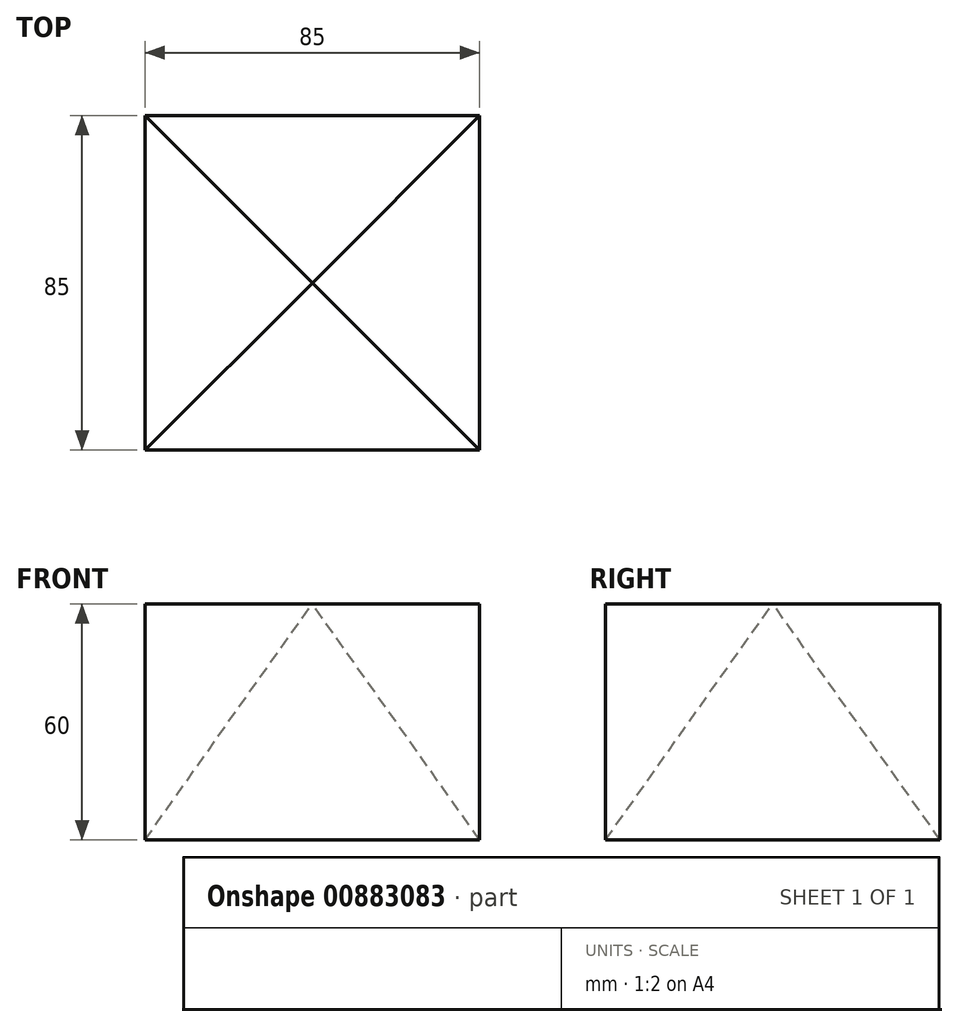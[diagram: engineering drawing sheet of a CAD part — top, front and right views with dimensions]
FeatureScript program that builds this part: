
annotation { "Feature Type Name" : "Feature", "Feature Type Description" : "" }
export const myFeature = defineFeature(function(context is Context, id is Id, definition is map)
    precondition{}
    {
        {
            var Q0;
            Q0=qCreatedBy(makeId("Top.planeOp"),FACE);
            var sketch = newSketch(context, id + "F0", { "sketchPlane" : qUnion([Q0])});
            skCircle(sketch, "E0.cCircle", {"center": v(0, 0) * mm, "radius": 42.5 * mm, "construction": true});
            skLineSegment(sketch, "E0.0", {"start": v(-42.5, 42.5) * mm, "end": v(42.5, 42.5) * mm});
            skLineSegment(sketch, "E0.1", {"start": v(42.5, 42.5) * mm, "end": v(42.5, -42.5) * mm});
            skLineSegment(sketch, "E0.2", {"start": v(42.5, -42.5) * mm, "end": v(-42.5, -42.5) * mm});
            skLineSegment(sketch, "E0.3", {"start": v(-42.5, -42.5) * mm, "end": v(-42.5, 42.5) * mm});
            skPoint(sketch, "E0.0.midPoint", {"position": v(0, 42.5) * mm});
            skSolve(sketch);
        }
        {
            var Q0;
            Q0=qCreatedBy(makeId("Top.planeOp"),FACE);
            cPlane(context, id + "F1", {"entities" : qUnion([Q0]), "cplaneType" : CPlaneType.OFFSET, "offset" : 60 * mm, "width" : 150 * mm, "height" : 150 * mm});
        }
        {
            var Q0;
            Q0=qCreatedBy(id+"F1.planeOp",FACE);
            var sketch = newSketch(context, id + "F2", { "sketchPlane" : qUnion([Q0])});
            skPoint(sketch, "E1", {"position": v(0, 0) * mm});
            skSolve(sketch);
        }
        {
            var Q0;
            Q0=makeQuery(id+"F0.imprint","IMPRINT",FACE,{"disambiguationData":[TD([[makeQuery(id+"F0.imprint","IMPRINT",EDGE,{"derivedFrom":sQuery(id+"F0.wireOp",EDGE,"E0.0")}),-1.0]])]});
            var Q1;
            Q1=sQuery(id+"F2.wireOp",VERTEX,"E1");
            loft(context, id + "F3", {"sheetProfilesArray" : [{ "sheetProfileEntities" : qUnion([Q0]) }, { "sheetProfileEntities" : qUnion([Q1]) }]});
        }
        {
            var Q0;
            Q0=qCreatedBy(id+"F1.planeOp",FACE);
            var sketch = newSketch(context, id + "F4", { "sketchPlane" : qUnion([Q0])});
            skCircle(sketch, "E2.cCircle", {"center": v(0, 0) * mm, "radius": 42.5 * mm, "construction": true});
            skLineSegment(sketch, "E2.0", {"start": v(-42.5, 42.5) * mm, "end": v(42.5, 42.5) * mm});
            skLineSegment(sketch, "E2.1", {"start": v(42.5, 42.5) * mm, "end": v(42.5, -42.5) * mm});
            skLineSegment(sketch, "E2.2", {"start": v(42.5, -42.5) * mm, "end": v(-42.5, -42.5) * mm});
            skLineSegment(sketch, "E2.3", {"start": v(-42.5, -42.5) * mm, "end": v(-42.5, 42.5) * mm});
            skPoint(sketch, "E2.0.midPoint", {"position": v(0, 42.5) * mm});
            skLineSegment(sketch, "E3", {"start": v(-42.5, 42.5) * mm, "end": v(42.5, -42.5) * mm});
            skLineSegment(sketch, "E4", {"start": v(42.5, 42.5) * mm, "end": v(-42.5, -42.5) * mm});
            skSolve(sketch);
        }
        {
            var Q0;
            {var subQ0=sQuery(id+"F4.wireOp",EDGE,"E2.3");Q0=makeQuery(id+"F4.imprint","IMPRINT",FACE,{"disambiguationData":[TD([[makeQuery(id+"F4.imprint","IMPRINT",EDGE,{"derivedFrom":subQ0}),-1.0]])]});}
            var Q1;
            Q1=makeQuery(id+"F3.opLoft","SWEPT_FACE",FACE,{"disambiguationData":[OSD([sQuery(id+"F0.wireOp",EDGE,"E0.0"),sQuery(id+"F0.wireOp",EDGE,"E0.2"),sQuery(id+"F0.wireOp",EDGE,"E0.3")])]});
            loft(context, id + "F5", {"sheetProfilesArray" : [{ "sheetProfileEntities" : qUnion([Q0]) }, { "sheetProfileEntities" : qUnion([Q1]) }]});
        }
        {
            var Q1;
            {var subQ0=sQuery(id+"F4.wireOp",EDGE,"E2.0");Q1=makeQuery(id+"F4.imprint","IMPRINT",FACE,{"disambiguationData":[TD([[makeQuery(id+"F4.imprint","IMPRINT",EDGE,{"derivedFrom":subQ0}),-1.0]])]});}
            var Q2;
            Q2=makeQuery(id+"F3.opLoft","SWEPT_FACE",FACE,{"disambiguationData":[OSD([sQuery(id+"F0.wireOp",EDGE,"E0.0"),sQuery(id+"F0.wireOp",EDGE,"E0.1"),sQuery(id+"F0.wireOp",EDGE,"E0.3")])]});
            loft(context, id + "F6", {"sheetProfilesArray" : [{ "sheetProfileEntities" : qUnion([Q1]) }, { "sheetProfileEntities" : qUnion([Q2]) }]});
        }
        {
            var Q0;
            {var subQ0=sQuery(id+"F4.wireOp",EDGE,"E2.1");Q0=makeQuery(id+"F4.imprint","IMPRINT",FACE,{"disambiguationData":[TD([[makeQuery(id+"F4.imprint","IMPRINT",EDGE,{"derivedFrom":subQ0}),-1.0]])]});}
            var Q1;
            Q1=makeQuery(id+"F3.opLoft","SWEPT_FACE",FACE,{"disambiguationData":[OSD([sQuery(id+"F0.wireOp",EDGE,"E0.0"),sQuery(id+"F0.wireOp",EDGE,"E0.1"),sQuery(id+"F0.wireOp",EDGE,"E0.2")])]});
            loft(context, id + "F7", {"sheetProfilesArray" : [{ "sheetProfileEntities" : qUnion([Q0]) }, { "sheetProfileEntities" : qUnion([Q1]) }]});
        }
        {
            var Q1;
            {var subQ0=sQuery(id+"F4.wireOp",EDGE,"E2.2");Q1=makeQuery(id+"F4.imprint","IMPRINT",FACE,{"disambiguationData":[TD([[makeQuery(id+"F4.imprint","IMPRINT",EDGE,{"derivedFrom":subQ0}),-1.0]])]});}
            var Q2;
            Q2=makeQuery(id+"F3.opLoft","SWEPT_FACE",FACE,{"disambiguationData":[OSD([sQuery(id+"F0.wireOp",EDGE,"E0.1"),sQuery(id+"F0.wireOp",EDGE,"E0.2"),sQuery(id+"F0.wireOp",EDGE,"E0.3")])]});
            loft(context, id + "F8", {"sheetProfilesArray" : [{ "sheetProfileEntities" : qUnion([Q1]) }, { "sheetProfileEntities" : qUnion([Q2]) }]});
        }
    });
